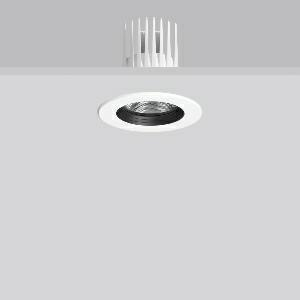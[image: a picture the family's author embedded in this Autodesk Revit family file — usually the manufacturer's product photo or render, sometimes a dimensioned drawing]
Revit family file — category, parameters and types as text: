
# Revit family: heledon_mini_e_901740_002_2_76_cff2
name_source: partatom
category: Lighting Fixtures
units: mm (PartAtom-declared; Revit-internal decimal feet)

## family parameters
Cut with Voids When Loaded = No
Host = Face
Light Source = No
Part Type = Normal
Room Calculation Point = No
Round Connector Dimension = Use Diameter
Shared = No

## types (1)
- HELEDON mini E (1 x LED Modul 927, 2400 lm, 2700)
    Apparent Load = 20 VA
    Approval mark = CE
    CIE Flux Codes = 100 100 100 100 100
    Color Rendering = 92
    Color Temperature = 2700
    Default Elevation = 1800 mm
    Description = Series: HELEDON mini
Round recessed downlight. Housing: die-cast aluminium, powder-coated. Black plastic ring and recessed LED to prevent glare from the side. Optical assembly with reflector made of MIRO-Silver with 98% total light reflection for outstanding efficiency - can be changed without tools. Best colour rendering index Ra>90. Suitable for Recessed ceiling mounting. Installation without tools thanks to spring fastening system. Including separate LED converter with connecting cable 600 mm.High quality converter without flickering and stroboscopic effect. Through-wiring box (5 pole) available as accessory. The following accessories can be mounted without use of tools: interchangeable lenses, decorative glasses, honeycomb louvre, clear and frosted diffusers, white interchangeable plastic ring. 
Colour: traffic white, matt (RAL 9016)
Diameter: 124 mm
Height: 3 mm
Cut-out diameter: 114 mm
Recess height: 170 mm
Luminaire: recess height: 120 mm
Lamp: LED
Socket: without socket
Colour temperature: 2700K
Colour rendering index (CRI): 92
System power: 20 W
Rated luminous flux: 2400 lm
Luminous efficiency: 120 lm/W
Control gear: Converter, dimmable, DALI
Protection class: II
Type of protection: IP 20
    Height = 0 mm  [stored 0 ft]
    Lamp = 1 x LED Modul 927
    Lamp Light Flux = 2400 lm
    Lamp count = 1
    Length = 124 mm  [stored 0.406824 ft]
    Lifetime = 50000 h
    Luminous efficacy = 120 lm/W
    Manufacturer = RZB
    ModVariant = No
    Model = 901740.002.2.76
    Mounting Place = Ceiling
    Mounting Type = Recessed
    Number of Poles = 1
    OnlyDefault = Yes
    Power Factor = 1
    Product Name = HELEDON mini E
    Product group = Recessed downlights
    ProductGroupID = 402
    Protection Class = Protection class II
    Protection Degree = IP 20
    RLX_Detail_Level = 1
    RLX_Emergency_Light_Flux = 0 lm
    RLX_Emergency_Type = 0
    RLX_Emergency_Type_DB = No
    RlxData = <blob elided: 128401 chars, md5=308f7c10>
    Socket = socket
    Standby Power = 0 W
    System Light Flux = 2400 lm
    System Power = 20 W
    Type Comments = Product without accessories
    Type Image = 901657.002.jpg
    URL = http://relux.com
    VarID = ---
    Voltage = 230 V
    Voltage Range = 220-240 V
    Weight = 0.00 kg
    Width = 0 mm  [stored 0 ft]

note: [stored X ft] marks values corroborated as IEEE doubles in the binary element streams (Revit-internal decimal feet)

## geometry (parser evidence)
native form markers: Blend x4, Sweep x11
no freeform markers — native parametric forms only
